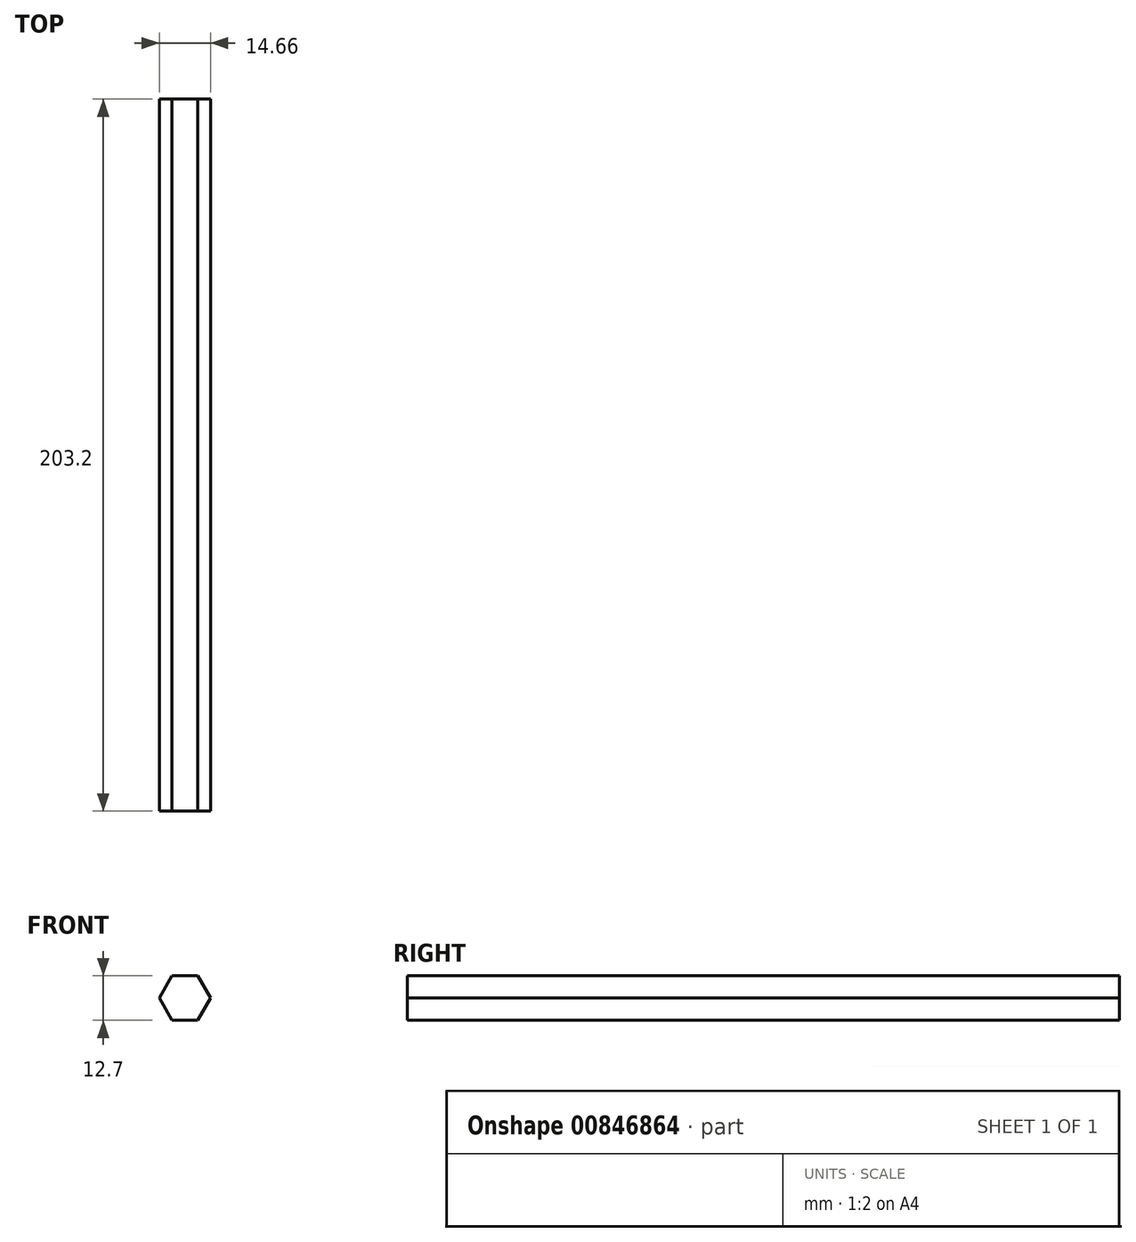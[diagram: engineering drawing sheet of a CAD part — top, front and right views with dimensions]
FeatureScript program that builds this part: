
annotation { "Feature Type Name" : "Feature", "Feature Type Description" : "" }
export const myFeature = defineFeature(function(context is Context, id is Id, definition is map)
    precondition{}
    {
        {
            var Q0;
            Q0=qCreatedBy(makeId("Front.planeOp"),FACE);
            var sketch = newSketch(context, id + "F0", { "sketchPlane" : qUnion([Q0])});
            skCircle(sketch, "E0.cCircle", {"center": v(0, 0) * mm, "radius": 6.35 * mm, "construction": true});
            skLineSegment(sketch, "E0.0", {"start": v(-3.67, 6.35) * mm, "end": v(3.67, 6.35) * mm});
            skLineSegment(sketch, "E0.1", {"start": v(3.67, 6.35) * mm, "end": v(7.33, 0) * mm});
            skLineSegment(sketch, "E0.2", {"start": v(7.33, 0) * mm, "end": v(3.67, -6.35) * mm});
            skLineSegment(sketch, "E0.3", {"start": v(3.67, -6.35) * mm, "end": v(-3.67, -6.35) * mm});
            skLineSegment(sketch, "E0.4", {"start": v(-3.67, -6.35) * mm, "end": v(-7.33, 0) * mm});
            skLineSegment(sketch, "E0.5", {"start": v(-7.33, 0) * mm, "end": v(-3.67, 6.35) * mm});
            skPoint(sketch, "E0.0.midPoint", {"position": v(0, 6.35) * mm});
            skSolve(sketch);
        }
        {
            var Q0;
            Q0=qSketchRegion(id+"F0",true);
            extrude(context, id + "F1", {"entities" : qUnion([Q0]), "endBound" : BoundingType.SYMMETRIC, "depth" : 203.2 * mm});
        }
    });
